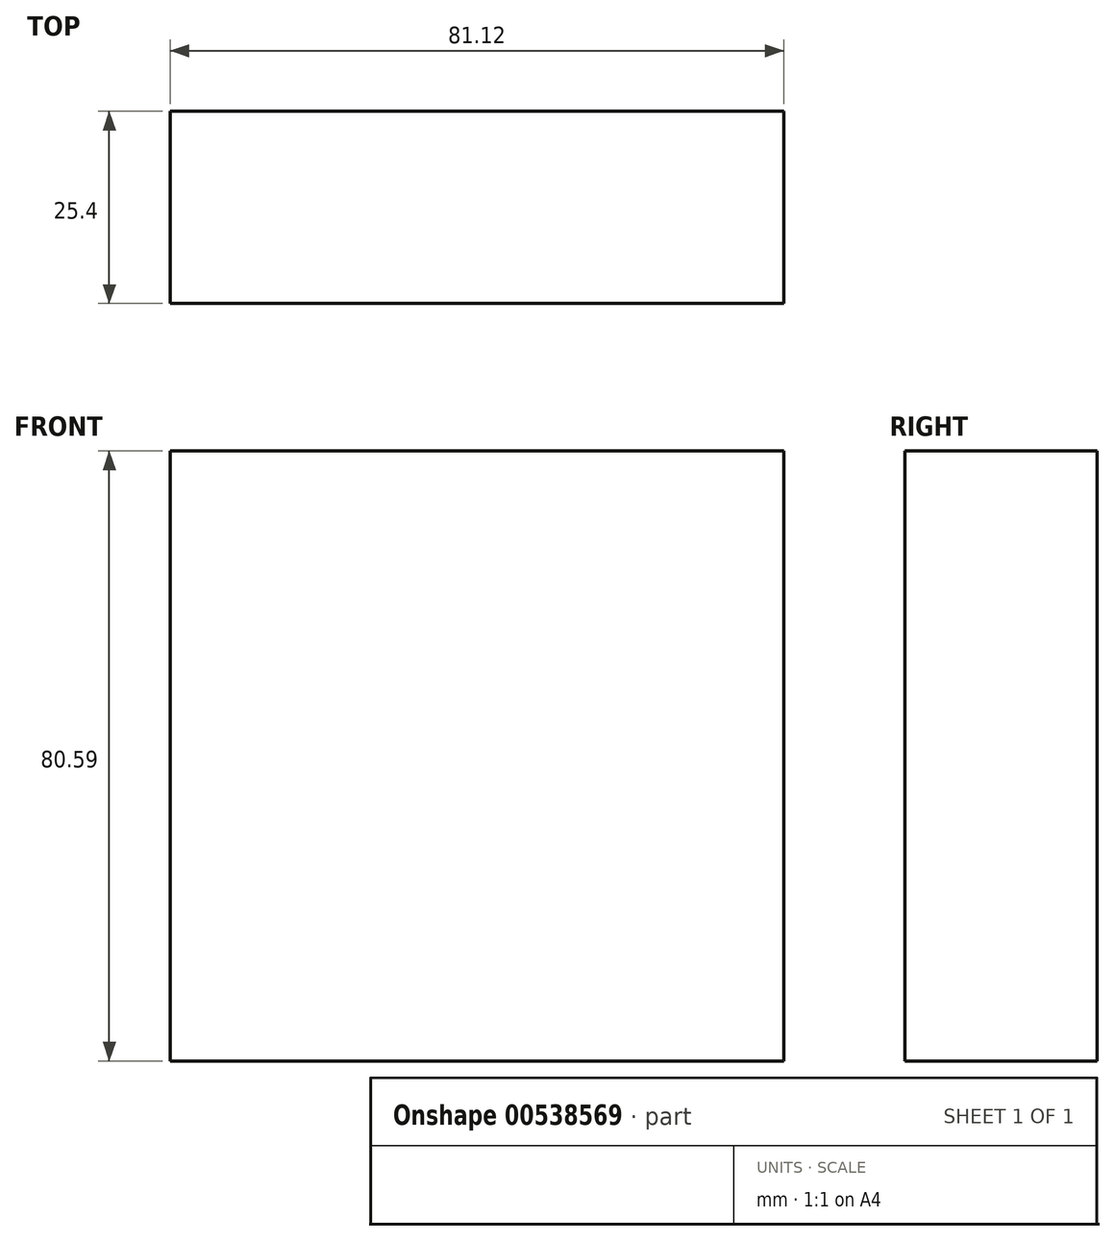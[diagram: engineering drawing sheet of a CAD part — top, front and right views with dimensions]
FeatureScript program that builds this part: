
annotation { "Feature Type Name" : "Feature", "Feature Type Description" : "" }
export const myFeature = defineFeature(function(context is Context, id is Id, definition is map)
    precondition{}
    {
        {
            var Q0;
            Q0=qCreatedBy(makeId("Front.planeOp"),FACE);
            var sketch = newSketch(context, id + "F0", { "sketchPlane" : qUnion([Q0])});
            skLineSegment(sketch, "E0.bottom", {"start": v(28.05, 41.84) * mm, "end": v(-53.07, 41.84) * mm});
            skLineSegment(sketch, "E0.top", {"start": v(28.05, -38.75) * mm, "end": v(-53.07, -38.75) * mm});
            skLineSegment(sketch, "E0.left", {"start": v(28.05, 41.84) * mm, "end": v(28.05, -38.75) * mm});
            skLineSegment(sketch, "E0.right", {"start": v(-53.07, 41.84) * mm, "end": v(-53.07, -38.75) * mm});
            skLineSegment(sketch, "E1.bottom", {"start": v(-12.51, 41.84) * mm, "end": v(66.78, 41.84) * mm});
            skLineSegment(sketch, "E1.top", {"start": v(-12.51, 87.93) * mm, "end": v(66.78, 87.93) * mm});
            skLineSegment(sketch, "E1.left", {"start": v(-12.51, 41.84) * mm, "end": v(-12.51, 87.93) * mm});
            skLineSegment(sketch, "E1.right", {"start": v(66.78, 41.84) * mm, "end": v(66.78, 87.93) * mm});
            skSolve(sketch);
        }
        {
            var Q0;
            {var subQ1=sQuery(id+"F0.wireOp",EDGE,"E0.bottom");Q0=makeQuery(id+"F0.imprint","IMPRINT",FACE,{"disambiguationData":[TD([[makeQuery(id+"F0.imprint","IMPRINT",EDGE,{"derivedFrom":subQ1}),1.0]])]});}
            var Q1;
            Q1=sQuery(id+"F0.wireOp",EDGE,"E0.left");
            extrude(context, id + "F1", {"entities" : qUnion([Q0]), "surfaceEntities" : qUnion([Q1]), "oppositeDirection" : true, "depth" : 25.4 * mm, "offsetDistance" : 25.4 * mm});
        }
    });
